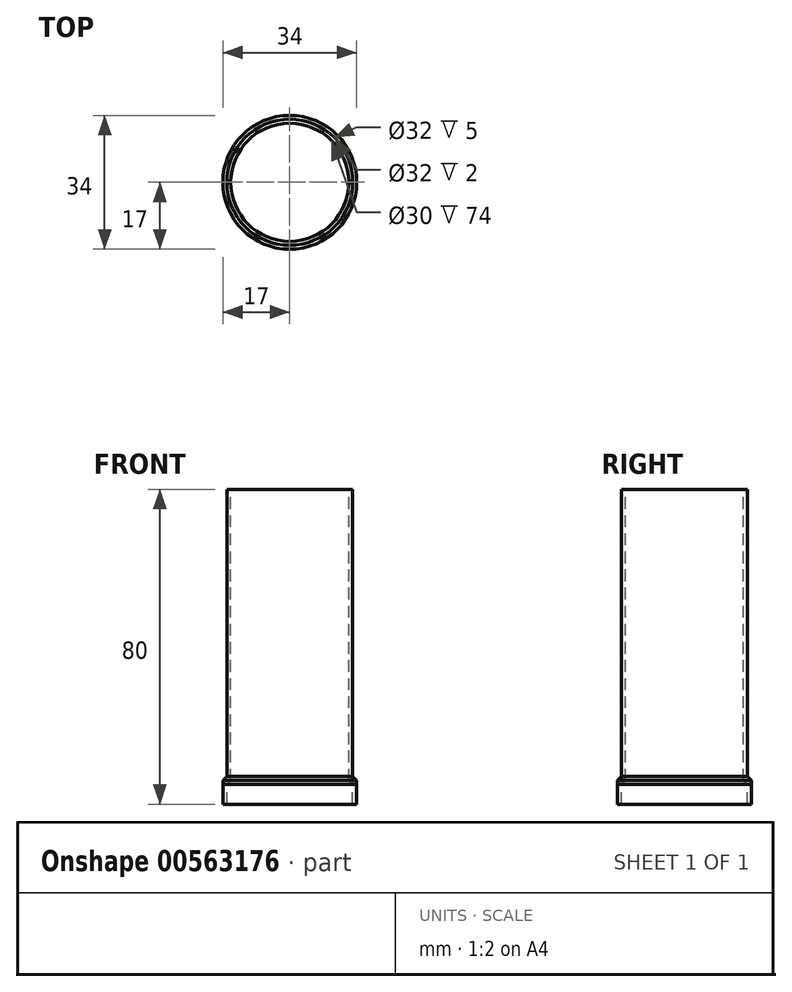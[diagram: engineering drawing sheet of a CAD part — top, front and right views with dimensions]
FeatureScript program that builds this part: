
annotation { "Feature Type Name" : "Feature", "Feature Type Description" : "" }
export const myFeature = defineFeature(function(context is Context, id is Id, definition is map)
    precondition{}
    {
        {
            var Q0;
            Q0=qCreatedBy(makeId("Top.planeOp"),FACE);
            var sketch = newSketch(context, id + "F0", { "sketchPlane" : qUnion([Q0])});
            skCircle(sketch, "E0", {"center": v(0, 0) * mm, "radius": 16 * mm});
            skCircle(sketch, "E1", {"center": v(0, 0) * mm, "radius": 15 * mm});
            skSolve(sketch);
        }
        {
            var Q0;
            Q0 = qSketchRegion(id + "F0", true);
            extrude(context, id + "F1", {"entities" : qUnion([Q0]), "oppositeDirection" : true, "depth" : 75 * mm, "offsetDistance" : 25 * mm});
        }
        {
            var Q0;
            Q0=makeQuery(id+"F1.opExtrude","CAP_FACE",FACE,{"disambiguationData":[OSD([sQuery(id+"F0.wireOp",EDGE,"E0"),sQuery(id+"F0.wireOp",EDGE,"E1")])],"isStart":false});
            var sketch = newSketch(context, id + "F2", { "sketchPlane" : qUnion([Q0])});
            skCircle(sketch, "E2", {"center": v(0, 0) * mm, "radius": 17 * mm});
            skCircle(sketch, "E3", {"center": v(0, 0) * mm, "radius": 16 * mm});
            skSolve(sketch);
        }
        {
            var Q0;
            Q0 = qSketchRegion(id + "F2", true);
            extrude(context, id + "F3", {"entities" : qUnion([Q0]), "depth" : 5 * mm, "offsetDistance" : 25 * mm});
        }
        {
            var Q0;
            Q0=makeQuery(id+"F3.opExtrude","CAP_FACE",FACE,{"disambiguationData":[OSD([sQuery(id+"F2.wireOp",EDGE,"E2"),sQuery(id+"F2.wireOp",EDGE,"E3")])],"isStart":true});
            extrude(context, id + "F4", {"entities" : qUnion([Q0]), "depth" : 2 * mm, "offsetDistance" : 25 * mm});
        }
        {
            var Q0;
            Q0=makeQuery(id+"F1.opExtrude","CAP_EDGE",EDGE,{"disambiguationData":[OSD([sQuery(id+"F0.wireOp",EDGE,"E1")])],"isStart":false});
            chamfer(context, id + "F5", {"entities" : qUnion([Q0]), "width" : 1 * mm, "tangentPropagation" : true});
        }
        {
            var Q0;
            Q0=makeQuery(id+"F4.opExtrude","CAP_EDGE",EDGE,{"disambiguationData":[OSD([sQuery(id+"F2.wireOp",EDGE,"E2")])],"isStart":false});
            chamfer(context, id + "F6", {"entities" : qUnion([Q0]), "width" : 1 * mm, "tangentPropagation" : true});
        }
    });
